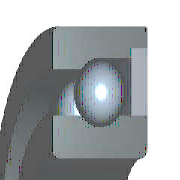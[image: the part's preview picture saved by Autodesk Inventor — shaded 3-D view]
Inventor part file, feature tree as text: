
AUTODESK INVENTOR PART (.ipt)
format: ipt  version: 2015 (Build 190159000, 159)  size: 307,712 bytes
history: native  units: mm (DEFAULTED — no unit token found)
features: sketch x1, other x1, pattern_circular x1
ambient origin geometry x8: Origin, YZ Plane, XZ Plane, XY Plane, X Axis, Y Axis, Z Axis, Center Point
bodies: Body (feature_tree)
feature tree (3):
  sketch  "Sketch"  dims[d0=2.86mm d55=90.0deg d1=0.3mm d2=0.1mm d58=90.0deg d3=70.0mm d4=360.0deg d5=0.0mm d6=0.0mm d7=0.0mm d8=8.0mm d9=13.5mm d10=19.0mm d11=17.178mm d12=11.586mm d13=6.0mm d14=6.0mm d15=5.0mm d16=3.0mm d17=0.0mm d18=0.0mm]
  other  "Ball"
  pattern_circular  "Balls"  Angle=90.0deg  [1 undecoded]
note: 1 required parameter value undecoded (feature->parameter linkage not recoverable at this tier; creation-order binding heuristic only, values carry confidence <= 0.55)
